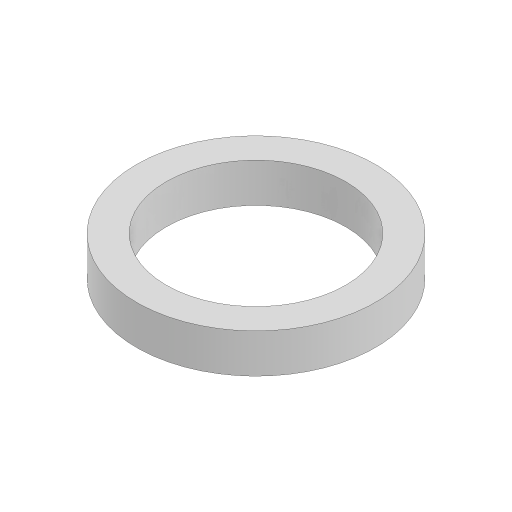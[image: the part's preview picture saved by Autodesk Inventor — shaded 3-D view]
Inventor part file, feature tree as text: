
AUTODESK INVENTOR PART (.ipt)
format: ipt  version: 2024 (Build 280153000, 153)  size: 95,232 bytes
history: native  units: in
note: dims shown in document units (in); Inventor stores cm internally (conversion verified against a paired STEP export)
features: extrude x1, direct_edit x1, sketch x1, other x1
ambient origin geometry x8: Origin, YZ Plane, XZ Plane, XY Plane, X Axis, Y Axis, Z Axis, Center Point
bodies: Solid1 (feature_tree)
feature tree (4):
  extrude  "Extrusion1"  Depth=0.25in
  direct_edit  "Direct Edit1"
  sketch  "Sketch1"  dims[d0=1.125in d1=0.2in d2=0.25in d3=0.0in d4=-0.01in]
  other  "Size1"
